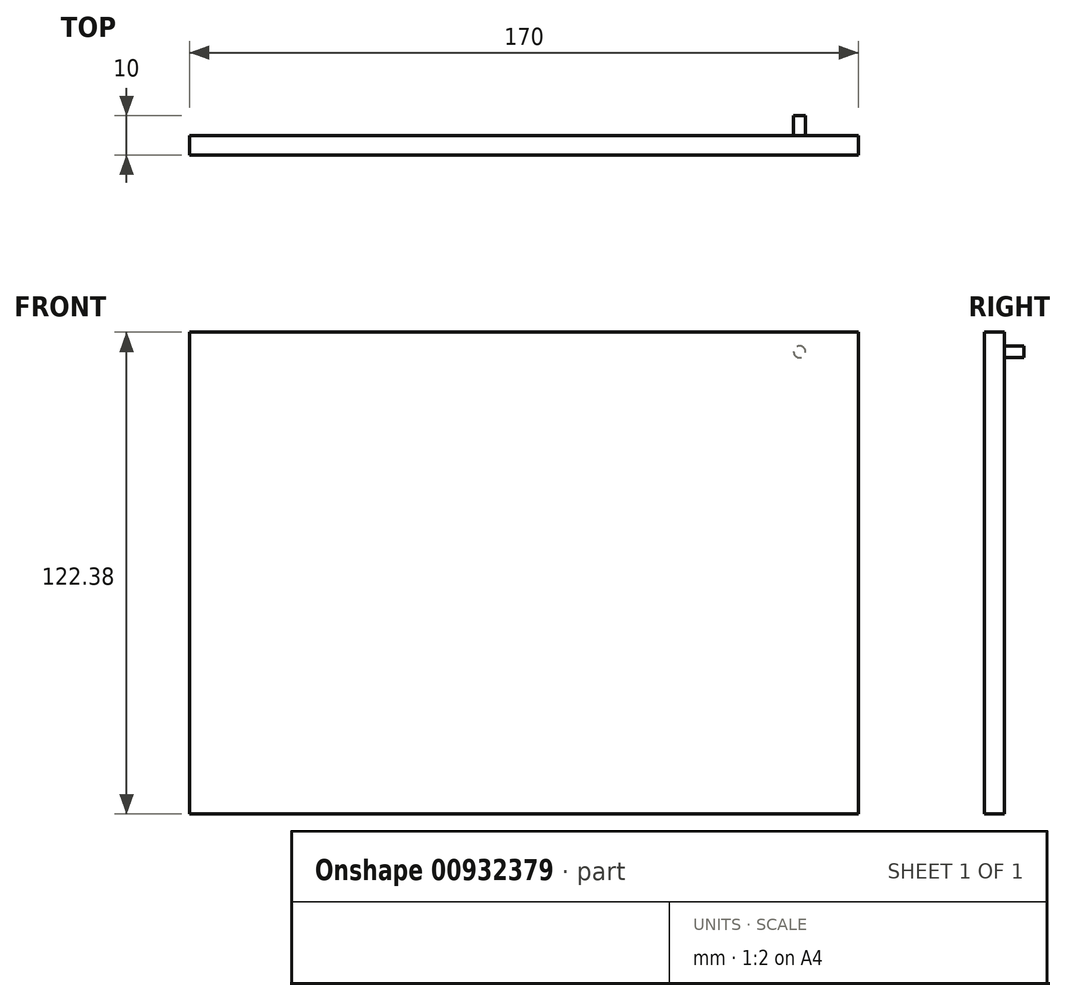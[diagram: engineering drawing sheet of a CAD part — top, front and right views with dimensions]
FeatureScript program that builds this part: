
annotation { "Feature Type Name" : "Feature", "Feature Type Description" : "" }
export const myFeature = defineFeature(function(context is Context, id is Id, definition is map)
    precondition{}
    {
        {
            var Q0;
            Q0=qCreatedBy(makeId("Front.planeOp"),FACE);
            var sketch = newSketch(context, id + "F0", { "sketchPlane" : qUnion([Q0])});
            skLineSegment(sketch, "E0.bottom", {"start": v(85, 61.19) * mm, "end": v(-85, 61.19) * mm});
            skLineSegment(sketch, "E0.top", {"start": v(85, -61.19) * mm, "end": v(-85, -61.19) * mm});
            skLineSegment(sketch, "E0.left", {"start": v(85, 61.19) * mm, "end": v(85, -61.19) * mm});
            skLineSegment(sketch, "E0.right", {"start": v(-85, 61.19) * mm, "end": v(-85, -61.19) * mm});
            skPoint(sketch, "E0.middle", {"position": v(0, 0) * mm});
            skSolve(sketch);
        }
        {
            var Q0;
            Q0 = qSketchRegion(id + "F0", true);
            extrude(context, id + "F1", {"entities" : qUnion([Q0]), "depth" : 5 * mm, "offsetDistance" : 25 * mm});
        }
        {
            var Q0;
            Q0=qCreatedBy(makeId("Front.planeOp"),FACE);
            var sketch = newSketch(context, id + "F2", { "sketchPlane" : qUnion([Q0])});
            skCircle(sketch, "E1", {"center": v(70, 56.19) * mm, "radius": 1.5 * mm});
            skSolve(sketch);
        }
        {
            var Q0;
            Q0 = qSketchRegion(id + "F2", true);
            extrude(context, id + "F3", {"entities" : qUnion([Q0]), "operationType" : NewBodyOperationType.ADD, "oppositeDirection" : true, "depth" : 5 * mm, "offsetDistance" : 25 * mm});
        }
    });
